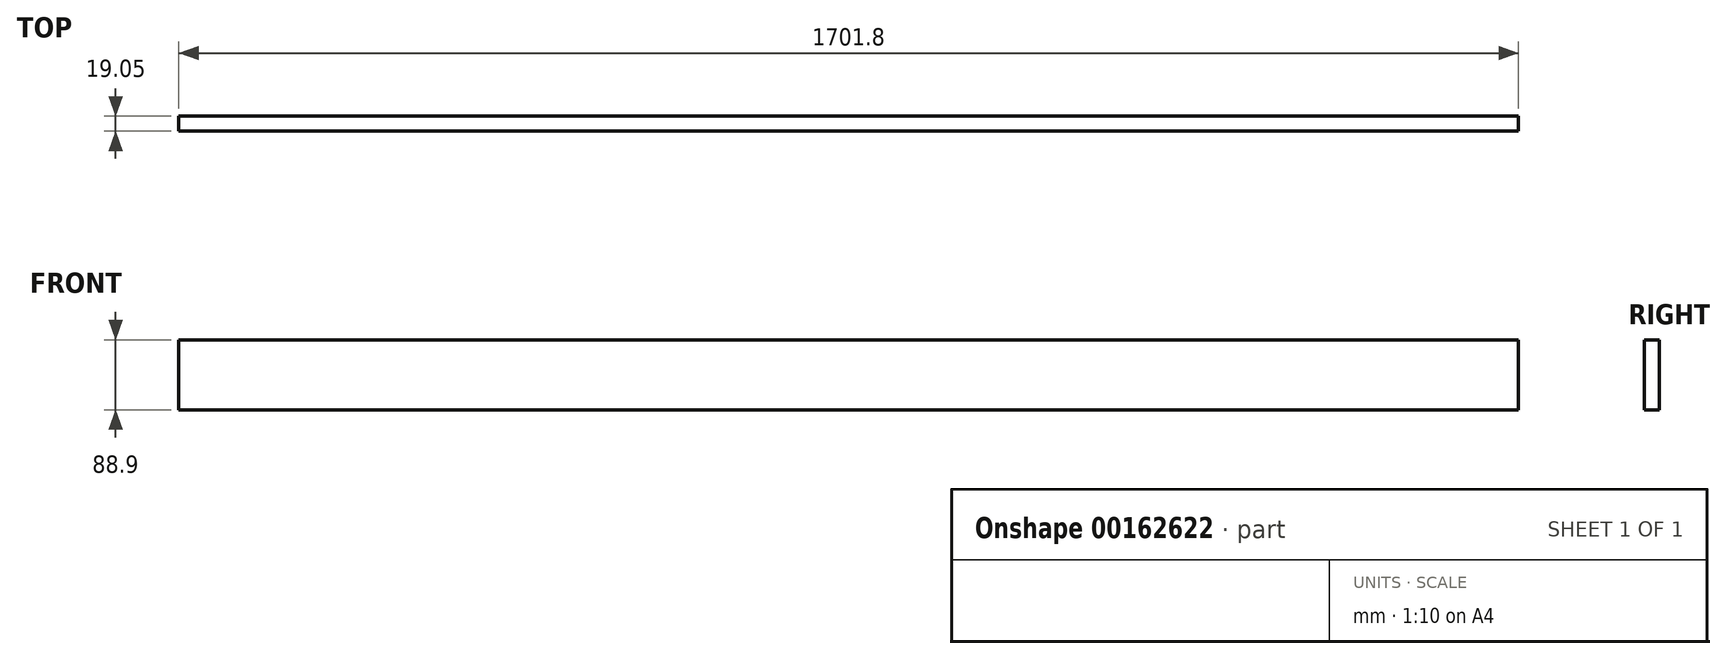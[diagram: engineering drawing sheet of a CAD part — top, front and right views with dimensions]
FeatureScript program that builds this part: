
annotation { "Feature Type Name" : "Feature", "Feature Type Description" : "" }
export const myFeature = defineFeature(function(context is Context, id is Id, definition is map)
    precondition{}
    {
        {
            var Q0;
            Q0=qCreatedBy(makeId("Front.planeOp"),FACE);
            var sketch = newSketch(context, id + "F0", { "sketchPlane" : qUnion([Q0])});
            skLineSegment(sketch, "E0.bottom", {"start": v(-850.33, -77.46) * mm, "end": v(851.47, -77.46) * mm});
            skLineSegment(sketch, "E0.top", {"start": v(-850.33, 11.44) * mm, "end": v(851.47, 11.44) * mm});
            skLineSegment(sketch, "E0.left", {"start": v(-850.33, -77.46) * mm, "end": v(-850.33, 11.44) * mm});
            skLineSegment(sketch, "E0.right", {"start": v(851.47, -77.46) * mm, "end": v(851.47, 11.44) * mm});
            skSolve(sketch);
        }
        {
            var Q0;
            Q0 = qSketchRegion(id + "F0", true);
            extrude(context, id + "F1", {"entities" : qUnion([Q0]), "depth" : 19.05 * mm});
        }
    });
